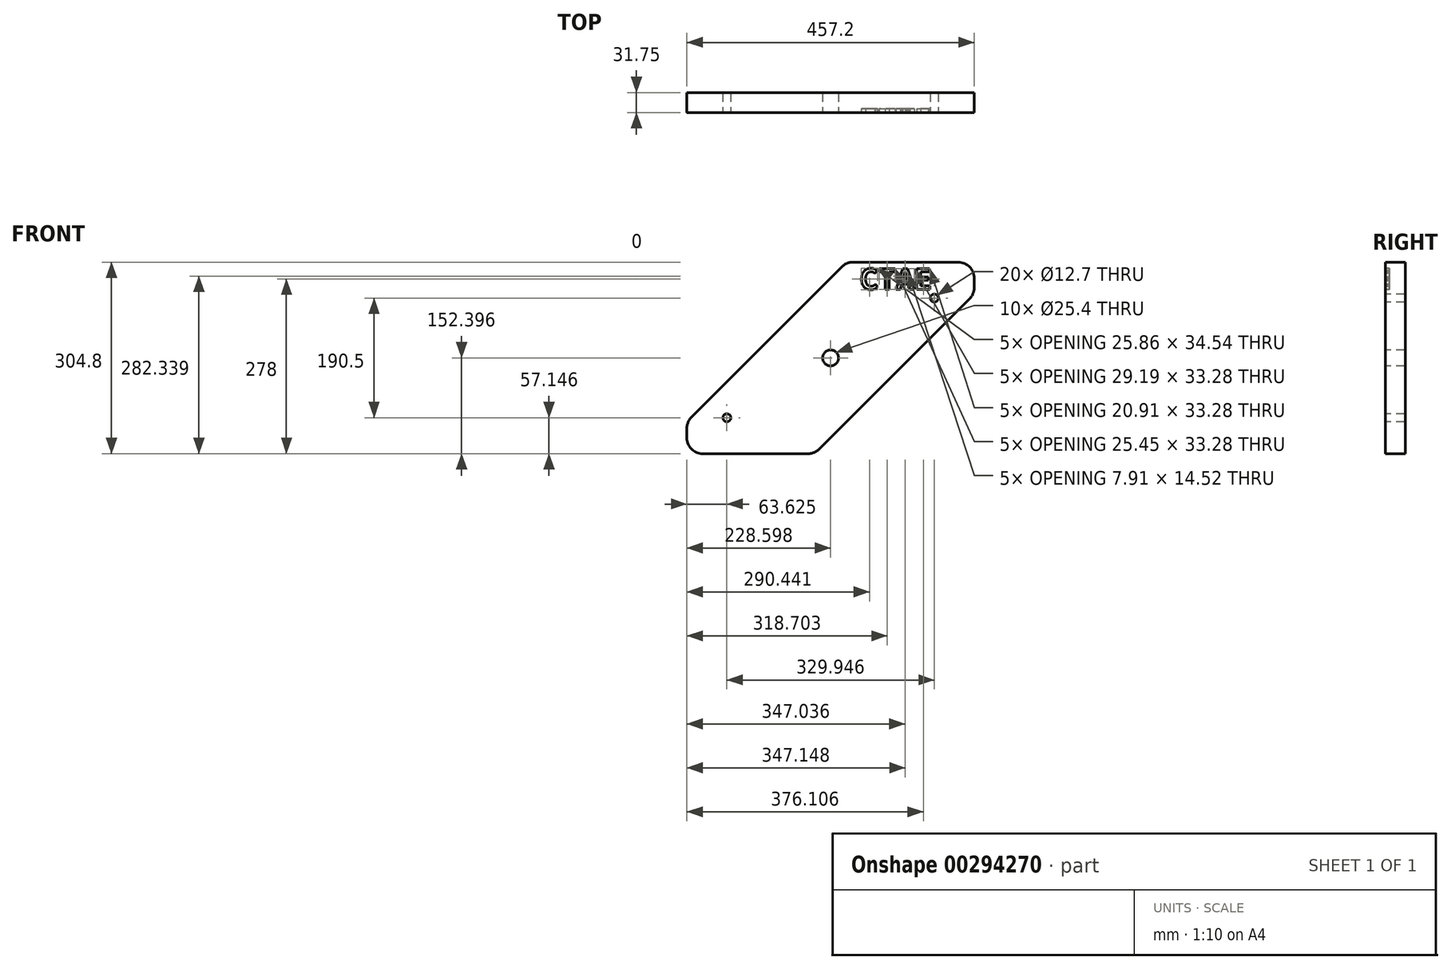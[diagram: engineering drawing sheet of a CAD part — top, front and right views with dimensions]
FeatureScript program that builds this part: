
annotation { "Feature Type Name" : "Feature", "Feature Type Description" : "" }
export const myFeature = defineFeature(function(context is Context, id is Id, definition is map)
    precondition{}
    {
        {
            var Q0;
            Q0=qCreatedBy(makeId("Front.planeOp"),FACE);
            var sketch = newSketch(context, id + "F0", { "sketchPlane" : qUnion([Q0])});
            skLineSegment(sketch, "E0.bottom", {"start": v(-215.93, 118.4) * mm, "end": v(241.27, 118.4) * mm});
            skLineSegment(sketch, "E0.top", {"start": v(-215.93, -186.4) * mm, "end": v(241.27, -186.4) * mm});
            skLineSegment(sketch, "E0.left", {"start": v(-215.93, 118.4) * mm, "end": v(-215.93, -186.4) * mm});
            skLineSegment(sketch, "E0.right", {"start": v(241.27, 118.4) * mm, "end": v(241.27, -186.4) * mm});
            skSolve(sketch);
        }
        {
            var Q0;
            Q0 = qSketchRegion(id + "F0", true);
            extrude(context, id + "F1", {"entities" : qUnion([Q0]), "depth" : 31.75 * mm});
        }
        {
            var Q0;
            Q0=makeQuery(id+"F1.opExtrude","SWEPT_EDGE",EDGE,{"disambiguationData":[OSD([sQuery(id+"F0.wireOp",EDGE,"E0.bottom"),sQuery(id+"F0.wireOp",EDGE,"E0.left")])]});
            var Q1;
            Q1=makeQuery(id+"F1.opExtrude","SWEPT_EDGE",EDGE,{"disambiguationData":[OSD([sQuery(id+"F0.wireOp",EDGE,"E0.top"),sQuery(id+"F0.wireOp",EDGE,"E0.right")])]});
            chamfer(context, id + "F2", {"entities" : qUnion([Q0, Q1]), "chamferType" : ChamferType.OFFSET_ANGLE, "width" : 254 * mm, "oppositeDirection" : false, "angle" : 45 * degree, "tangentPropagation" : true});
        }
        {
            var Q0;
            Q0=makeQuery(id+"F1.opExtrude","SWEPT_EDGE",EDGE,{"disambiguationData":[OSD([sQuery(id+"F0.wireOp",EDGE,"E0.top"),sQuery(id+"F0.wireOp",EDGE,"E0.left")])]});
            var Q1;
            Q1=makeQuery(id+"F1.opExtrude","SWEPT_EDGE",EDGE,{"disambiguationData":[OSD([sQuery(id+"F0.wireOp",EDGE,"E0.bottom"),sQuery(id+"F0.wireOp",EDGE,"E0.right")])]});
            var Q2;
            {var subQ0=sQuery(id+"F0.wireOp",EDGE,"E0.right");Q2=makeQuery(id+"F2.opChamfer","BLEND_EDGE",EDGE,{"blendedFrom":[makeQuery(id+"F1.opExtrude","SWEPT_EDGE",EDGE,{"disambiguationData":[OSD([sQuery(id+"F0.wireOp",EDGE,"E0.top"),subQ0])]}),makeQuery(id+"F1.opExtrude","SWEPT_FACE",FACE,{"disambiguationData":[OSD([subQ0])]})],"blendedInto":[makeQuery(id+"F1.opExtrude","SWEPT_FACE",FACE,{"disambiguationData":[OSD([subQ0])]})]});}
            var Q3;
            {var subQ0=sQuery(id+"F0.wireOp",EDGE,"E0.left");Q3=makeQuery(id+"F2.opChamfer","BLEND_EDGE",EDGE,{"blendedFrom":[makeQuery(id+"F1.opExtrude","SWEPT_EDGE",EDGE,{"disambiguationData":[OSD([sQuery(id+"F0.wireOp",EDGE,"E0.bottom"),subQ0])]}),makeQuery(id+"F1.opExtrude","SWEPT_FACE",FACE,{"disambiguationData":[OSD([subQ0])]})],"blendedInto":[makeQuery(id+"F1.opExtrude","SWEPT_FACE",FACE,{"disambiguationData":[OSD([subQ0])]})]});}
            var Q4;
            {var subQ0=sQuery(id+"F0.wireOp",EDGE,"E0.bottom");Q4=makeQuery(id+"F2.opChamfer","BLEND_EDGE",EDGE,{"blendedFrom":[makeQuery(id+"F1.opExtrude","SWEPT_EDGE",EDGE,{"disambiguationData":[OSD([subQ0,sQuery(id+"F0.wireOp",EDGE,"E0.left")])]}),makeQuery(id+"F1.opExtrude","SWEPT_FACE",FACE,{"disambiguationData":[OSD([subQ0])]})],"blendedInto":[makeQuery(id+"F1.opExtrude","SWEPT_FACE",FACE,{"disambiguationData":[OSD([subQ0])]})]});}
            var Q5;
            {var subQ0=sQuery(id+"F0.wireOp",EDGE,"E0.top");Q5=makeQuery(id+"F2.opChamfer","BLEND_EDGE",EDGE,{"blendedFrom":[makeQuery(id+"F1.opExtrude","SWEPT_EDGE",EDGE,{"disambiguationData":[OSD([subQ0,sQuery(id+"F0.wireOp",EDGE,"E0.right")])]}),makeQuery(id+"F1.opExtrude","SWEPT_FACE",FACE,{"disambiguationData":[OSD([subQ0])]})],"blendedInto":[makeQuery(id+"F1.opExtrude","SWEPT_FACE",FACE,{"disambiguationData":[OSD([subQ0])]})]});}
            fillet(context, id + "F3", {"entities" : qUnion([Q0, Q1, Q2, Q3, Q4, Q5]), "radius" : 25.4 * mm, "tangentPropagation" : true, "allowEdgeOverflow" : false});
        }
        {
            var Q0;
            Q0=makeQuery(id+"F1.opExtrude","CAP_FACE",FACE,{"disambiguationData":[OSD([sQuery(id+"F0.wireOp",EDGE,"E0.bottom"),sQuery(id+"F0.wireOp",EDGE,"E0.top"),sQuery(id+"F0.wireOp",EDGE,"E0.left"),sQuery(id+"F0.wireOp",EDGE,"E0.right")])],"isStart":false});
            var sketch = newSketch(context, id + "F4", { "sketchPlane" : qUnion([Q0])});
            skPoint(sketch, "E1", {"position": v(-152.3, -129.25) * mm});
            skPoint(sketch, "E2", {"position": v(12.67, -34) * mm});
            skPoint(sketch, "E3", {"position": v(177.64, 61.25) * mm});
            skSolve(sketch);
        }
        {
            var Q0;
            Q0=sQuery(id+"F4.wireOp",VERTEX,"E3");
            var Q1;
            Q1=sQuery(id+"F4.wireOp",VERTEX,"E1");
            var Q2;
            Q2=makeQuery(id+"F1.opExtrude","SWEPT_BODY",BODY,{"disambiguationData":[OSD([sQuery(id+"F0.wireOp",EDGE,"E0.bottom"),sQuery(id+"F0.wireOp",EDGE,"E0.top"),sQuery(id+"F0.wireOp",EDGE,"E0.left"),sQuery(id+"F0.wireOp",EDGE,"E0.right")])]});
            hole(context, id + "F5", {"style" : HoleStyle.SIMPLE, "endStyle" : HoleEndStyle.THROUGH, "holeDiameter" : 12.7 * mm, "tappedDepth" : 12.7 * mm, "tapClearance" : 3, "locations" : qUnion([Q0, Q1]), "scope" : qUnion([Q2])});
        }
        {
            var Q0;
            Q0=sQuery(id+"F4.wireOp",VERTEX,"E2");
            var Q1;
            Q1=makeQuery(id+"F1.opExtrude","SWEPT_BODY",BODY,{"disambiguationData":[OSD([sQuery(id+"F0.wireOp",EDGE,"E0.bottom"),sQuery(id+"F0.wireOp",EDGE,"E0.top"),sQuery(id+"F0.wireOp",EDGE,"E0.left"),sQuery(id+"F0.wireOp",EDGE,"E0.right")])]});
            hole(context, id + "F6", {"style" : HoleStyle.SIMPLE, "endStyle" : HoleEndStyle.THROUGH, "holeDiameter" : 25.4 * mm, "tappedDepth" : 12.7 * mm, "tapClearance" : 3, "locations" : qUnion([Q0]), "scope" : qUnion([Q1])});
        }
        {
            var Q0;
            {var subQ1=sQuery(id+"F0.wireOp",EDGE,"E0.bottom");Q0=makeQuery(id+"F4.imprint","IMPRINT",FACE,{"disambiguationData":[TD([[makeQuery(id+"F4.imprint","IMPRINT",EDGE,{"derivedFrom":makeQuery(id+"F1.opExtrude","CAP_EDGE",EDGE,{"disambiguationData":[OSD([subQ1])],"isStart":false})}),-1.0]])]});}
            var sketch = newSketch(context, id + "F7", { "sketchPlane" : qUnion([Q0])});
            skText(sketch, "E4", { "text": "CTAE", "fontName": "NotoSansCJKjp-Bold.otf"});
            const initialGuessF7  = {"E4": [0.05915, 0.07496, 1, 0, 0.03238]};
            skSetInitialGuess(sketch, initialGuessF7);
            skSolve(sketch);
        }
        {
            var Q0;
            Q0 = qSketchRegion(id + "F7", true);
            extrude(context, id + "F8", {"entities" : qUnion([Q0]), "operationType" : NewBodyOperationType.REMOVE, "oppositeDirection" : true, "depth" : 6.35 * mm});
        }
    });
